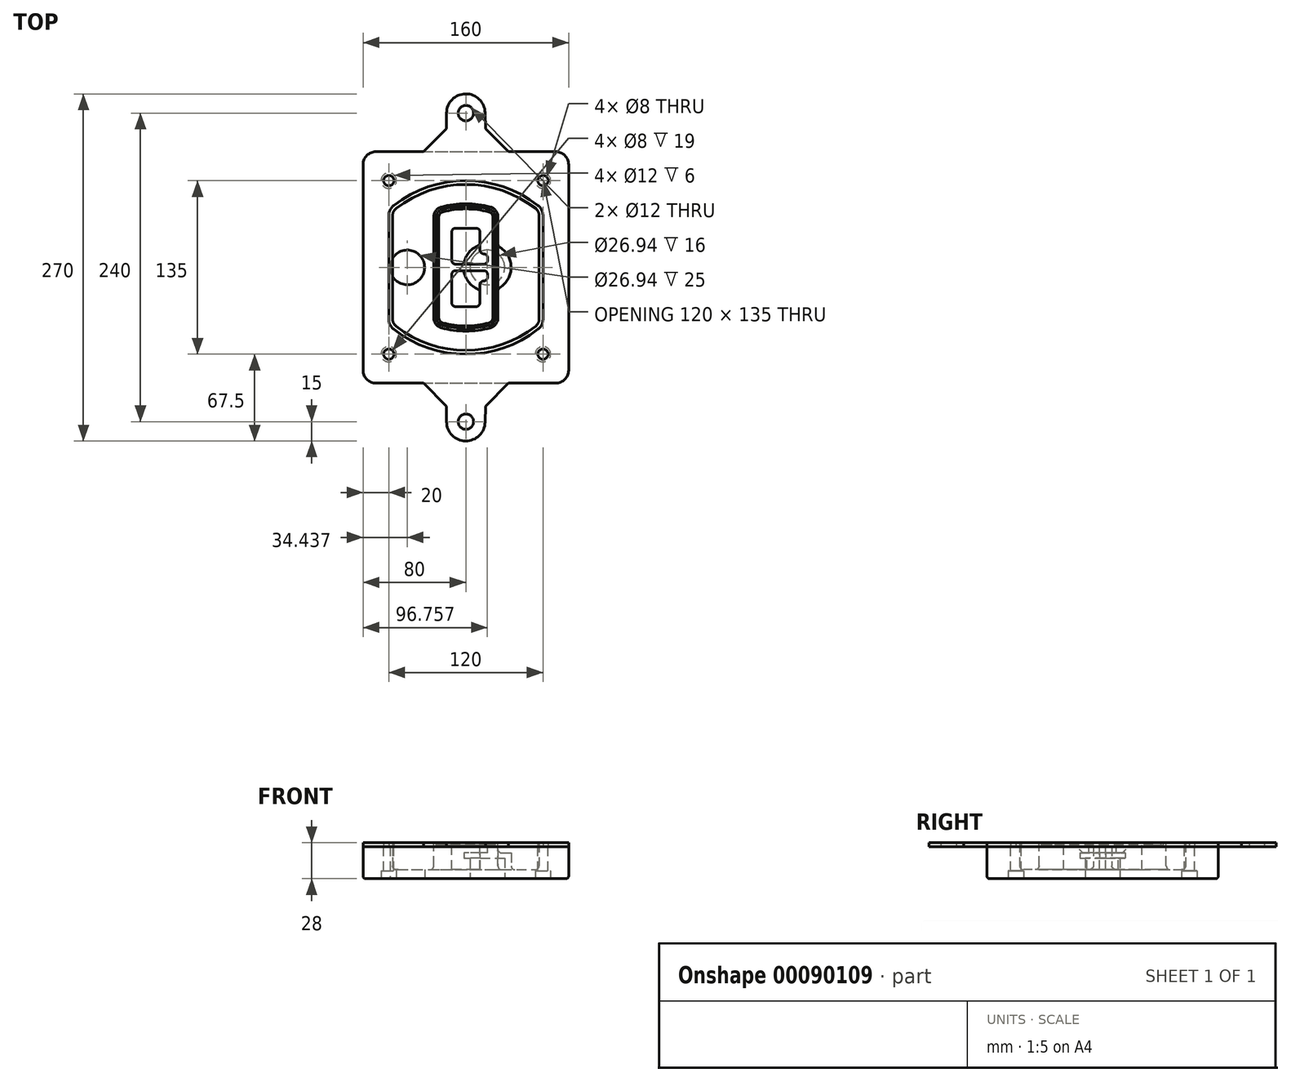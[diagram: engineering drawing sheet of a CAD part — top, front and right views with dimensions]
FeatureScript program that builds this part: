
annotation { "Feature Type Name" : "Feature", "Feature Type Description" : "" }
export const myFeature = defineFeature(function(context is Context, id is Id, definition is map)
    precondition{}
    {
        {
            var Q0;
            Q0=qCreatedBy(makeId("Top.planeOp"),FACE);
            var sketch = newSketch(context, id + "F0", { "sketchPlane" : qUnion([Q0])});
            skPoint(sketch, "E0.rect.middle", {"position": v(0, 0) * mm});
            skLineSegment(sketch, "E1.bottom", {"start": v(-70, -90) * mm, "end": v(70, -90) * mm});
            skLineSegment(sketch, "E1.top", {"start": v(-70, 90) * mm, "end": v(70, 90) * mm});
            skLineSegment(sketch, "E1.left", {"start": v(-80, -80) * mm, "end": v(-80, 80) * mm});
            skLineSegment(sketch, "E1.right", {"start": v(80, -80) * mm, "end": v(80, 80) * mm});
            skLineSegment(sketch, "E2", {"start": v(-80, 90) * mm, "end": v(80, -90) * mm, "construction": true});
            skLineSegment(sketch, "E3", {"start": v(80, 90) * mm, "end": v(-80, -90) * mm, "construction": true});
            skCircle(sketch, "E4", {"center": v(-60, 67.5) * mm, "radius": 4 * mm});
            skCircle(sketch, "E5", {"center": v(60, 67.5) * mm, "radius": 4 * mm});
            skCircle(sketch, "E6", {"center": v(60, -67.5) * mm, "radius": 4 * mm});
            skCircle(sketch, "E7", {"center": v(-60, -67.5) * mm, "radius": 4 * mm});
            skLineSegment(sketch, "E8", {"start": v(-60, 67.5) * mm, "end": v(60, 67.5) * mm, "construction": true});
            skLineSegment(sketch, "E9", {"start": v(60, 67.5) * mm, "end": v(60, -67.5) * mm, "construction": true});
            skLineSegment(sketch, "E10", {"start": v(60, -67.5) * mm, "end": v(-60, -67.5) * mm, "construction": true});
            skLineSegment(sketch, "E11", {"start": v(-60, -67.5) * mm, "end": v(-60, 67.5) * mm, "construction": true});
            skLineSegment(sketch, "E12", {"start": v(-60, 40.3) * mm, "end": v(-60, -40.3) * mm});
            skLineSegment(sketch, "E13", {"start": v(60, 40.3) * mm, "end": v(60, -40.3) * mm});
            skArc(sketch, "E14", {"start": v(56.15, 48.18) * mm, "mid": v(0, 67.5) * mm, "end": v(-56.15, 48.18) * mm});
            skArc(sketch, "E15", {"start": v(-56.15, -48.18) * mm, "mid": v(0, -67.5) * mm, "end": v(56.15, -48.18) * mm});
            skLineSegment(sketch, "E16", {"start": v(-60, 0) * mm, "end": v(60, 0) * mm, "construction": true});
            skPoint(sketch, "E17.visualSharp", {"position": v(-60, -45) * mm});
            skArc(sketch, "E17.filletArc", {"start": v(-60, -40.3) * mm, "mid": v(-58.99, -44.68) * mm, "end": v(-56.15, -48.18) * mm});
            skPoint(sketch, "E18.visualSharp", {"position": v(-60, 45) * mm});
            skArc(sketch, "E18.filletArc", {"start": v(-56.15, 48.18) * mm, "mid": v(-58.99, 44.68) * mm, "end": v(-60, 40.3) * mm});
            skPoint(sketch, "E19.visualSharp", {"position": v(60, 45) * mm});
            skArc(sketch, "E19.filletArc", {"start": v(60, 40.3) * mm, "mid": v(58.99, 44.68) * mm, "end": v(56.15, 48.18) * mm});
            skPoint(sketch, "E20.visualSharp", {"position": v(60, -45) * mm});
            skArc(sketch, "E20.filletArc", {"start": v(56.15, -48.18) * mm, "mid": v(58.99, -44.68) * mm, "end": v(60, -40.3) * mm});
            skPoint(sketch, "E21.visualSharp", {"position": v(-80, 90) * mm});
            skArc(sketch, "E21.filletArc", {"start": v(-70, 90) * mm, "mid": v(-77.07, 87.07) * mm, "end": v(-80, 80) * mm});
            skPoint(sketch, "E22.visualSharp", {"position": v(80, 90) * mm});
            skArc(sketch, "E22.filletArc", {"start": v(80, 80) * mm, "mid": v(77.07, 87.07) * mm, "end": v(70, 90) * mm});
            skPoint(sketch, "E23.visualSharp", {"position": v(80, -90) * mm});
            skArc(sketch, "E23.filletArc", {"start": v(70, -90) * mm, "mid": v(77.07, -87.07) * mm, "end": v(80, -80) * mm});
            skPoint(sketch, "E24.visualSharp", {"position": v(-80, -90) * mm});
            skArc(sketch, "E24.filletArc", {"start": v(-80, -80) * mm, "mid": v(-77.07, -87.07) * mm, "end": v(-70, -90) * mm});
            skArc(sketch, "E25.0", {"start": v(57, 40.3) * mm, "mid": v(56.3, 43.36) * mm, "end": v(54.3, 45.81) * mm});
            skLineSegment(sketch, "E25.1", {"start": v(57, 40.3) * mm, "end": v(57, -40.3) * mm});
            skArc(sketch, "E25.2", {"start": v(54.3, -45.81) * mm, "mid": v(56.3, -43.36) * mm, "end": v(57, -40.3) * mm});
            skArc(sketch, "E25.3", {"start": v(-54.3, -45.81) * mm, "mid": v(0, -64.5) * mm, "end": v(54.3, -45.81) * mm});
            skArc(sketch, "E25.4", {"start": v(-57, -40.3) * mm, "mid": v(-56.3, -43.36) * mm, "end": v(-54.3, -45.81) * mm});
            skArc(sketch, "E25.5", {"start": v(54.3, 45.81) * mm, "mid": v(0, 64.5) * mm, "end": v(-54.3, 45.81) * mm});
            skLineSegment(sketch, "E25.6", {"start": v(-57, 40.3) * mm, "end": v(-57, -40.3) * mm});
            skArc(sketch, "E25.7", {"start": v(-54.3, 45.81) * mm, "mid": v(-56.3, 43.36) * mm, "end": v(-57, 40.3) * mm});
            skArc(sketch, "E26.0", {"start": v(-58.62, 51.33) * mm, "mid": v(-62.58, 46.43) * mm, "end": v(-64, 40.3) * mm});
            skArc(sketch, "E26.1", {"start": v(58.62, 51.33) * mm, "mid": v(0, 71.5) * mm, "end": v(-58.62, 51.33) * mm});
            skArc(sketch, "E26.2", {"start": v(64, 40.3) * mm, "mid": v(62.58, 46.43) * mm, "end": v(58.62, 51.33) * mm});
            skLineSegment(sketch, "E26.3", {"start": v(64, 40.3) * mm, "end": v(64, -40.3) * mm});
            skArc(sketch, "E26.4", {"start": v(58.62, -51.33) * mm, "mid": v(62.58, -46.43) * mm, "end": v(64, -40.3) * mm});
            skLineSegment(sketch, "E26.5", {"start": v(-64, 40.3) * mm, "end": v(-64, -40.3) * mm});
            skArc(sketch, "E26.6", {"start": v(-58.62, -51.33) * mm, "mid": v(0, -71.5) * mm, "end": v(58.62, -51.33) * mm});
            skArc(sketch, "E26.7", {"start": v(-64, -40.3) * mm, "mid": v(-62.58, -46.43) * mm, "end": v(-58.62, -51.33) * mm});
            skSolve(sketch);
        }
        {
            var Q0;
            Q0=makeQuery(id+"F0.imprint","IMPRINT",FACE,{"disambiguationData":[TD([[makeQuery(id+"F0.imprint","IMPRINT",EDGE,{"derivedFrom":sQuery(id+"F0.wireOp",EDGE,"E1.bottom")}),1.0]])]});
            var Q1;
            Q1=makeQuery(id+"F0.imprint","IMPRINT",FACE,{"disambiguationData":[TD([[makeQuery(id+"F0.imprint","IMPRINT",EDGE,{"derivedFrom":sQuery(id+"F0.wireOp",EDGE,"E12")}),1.0]])]});
            var Q2;
            Q2=makeQuery(id+"F0.imprint","IMPRINT",FACE,{"disambiguationData":[TD([[makeQuery(id+"F0.imprint","IMPRINT",EDGE,{"derivedFrom":sQuery(id+"F0.wireOp",EDGE,"E25.0")}),1.0]])]});
            var Q3;
            Q3=makeQuery(id+"F0.imprint","IMPRINT",FACE,{"disambiguationData":[TD([[makeQuery(id+"F0.imprint","IMPRINT",EDGE,{"derivedFrom":sQuery(id+"F0.wireOp",EDGE,"E12")}),-1.0]])]});
            extrude(context, id + "F1", {"entities" : qUnion([Q0, Q1, Q2, Q3]), "oppositeDirection" : true, "depth" : 25 * mm});
        }
        {
            var Q0;
            Q0=makeQuery(id+"F0.imprint","IMPRINT",FACE,{"disambiguationData":[TD([[makeQuery(id+"F0.imprint","IMPRINT",EDGE,{"derivedFrom":sQuery(id+"F0.wireOp",EDGE,"E12")}),1.0]])]});
            extrude(context, id + "F2", {"entities" : qUnion([Q0]), "operationType" : NewBodyOperationType.ADD, "depth" : 3 * mm});
        }
        {
            var Q0;
            Q0=makeQuery(id+"F0.imprint","IMPRINT",FACE,{"disambiguationData":[TD([[makeQuery(id+"F0.imprint","IMPRINT",EDGE,{"derivedFrom":sQuery(id+"F0.wireOp",EDGE,"E25.0")}),1.0]])]});
            extrude(context, id + "F3", {"entities" : qUnion([Q0]), "operationType" : NewBodyOperationType.REMOVE, "oppositeDirection" : true, "depth" : 18 * mm});
        }
        {
            var Q0;
            Q0=makeQuery(id+"F2.opExtrude","CAP_FACE",FACE,{"disambiguationData":[OSD([sQuery(id+"F0.wireOp",EDGE,"E12"),sQuery(id+"F0.wireOp",EDGE,"E13"),sQuery(id+"F0.wireOp",EDGE,"E14"),sQuery(id+"F0.wireOp",EDGE,"E15"),sQuery(id+"F0.wireOp",EDGE,"E17.filletArc"),sQuery(id+"F0.wireOp",EDGE,"E18.filletArc"),sQuery(id+"F0.wireOp",EDGE,"E19.filletArc"),sQuery(id+"F0.wireOp",EDGE,"E20.filletArc"),sQuery(id+"F0.wireOp",EDGE,"E25.0"),sQuery(id+"F0.wireOp",EDGE,"E25.1"),sQuery(id+"F0.wireOp",EDGE,"E25.2"),sQuery(id+"F0.wireOp",EDGE,"E25.3"),sQuery(id+"F0.wireOp",EDGE,"E25.4"),sQuery(id+"F0.wireOp",EDGE,"E25.5"),sQuery(id+"F0.wireOp",EDGE,"E25.6"),sQuery(id+"F0.wireOp",EDGE,"E25.7")])],"isStart":false});
            var sketch = newSketch(context, id + "F4", { "sketchPlane" : qUnion([Q0])});
            skArc(sketch, "E27.0", {"start": v(-19.08, -46.97) * mm, "mid": v(0, -49.5) * mm, "end": v(19.08, -46.97) * mm});
            skArc(sketch, "E28.0", {"start": v(19.08, 46.97) * mm, "mid": v(0, 49.5) * mm, "end": v(-19.08, 46.97) * mm});
            skLineSegment(sketch, "E29", {"start": v(-25, 39.25) * mm, "end": v(-25, -39.25) * mm});
            skLineSegment(sketch, "E30", {"start": v(25, 39.25) * mm, "end": v(25, -39.25) * mm});
            skLineSegment(sketch, "E31", {"start": v(-25, 45.1) * mm, "end": v(25, 45.1) * mm, "construction": true});
            skLineSegment(sketch, "E32", {"start": v(-25, -45.1) * mm, "end": v(25, -45.1) * mm, "construction": true});
            skPoint(sketch, "E33.visualSharp", {"position": v(-25, 45.1) * mm});
            skArc(sketch, "E33.filletArc", {"start": v(-19.08, 46.97) * mm, "mid": v(-23.35, 44.11) * mm, "end": v(-25, 39.25) * mm});
            skPoint(sketch, "E34.visualSharp", {"position": v(25, 45.1) * mm});
            skArc(sketch, "E34.filletArc", {"start": v(25, 39.25) * mm, "mid": v(23.35, 44.11) * mm, "end": v(19.08, 46.97) * mm});
            skPoint(sketch, "E35.visualSharp", {"position": v(25, -45.1) * mm});
            skArc(sketch, "E35.filletArc", {"start": v(19.08, -46.97) * mm, "mid": v(23.35, -44.11) * mm, "end": v(25, -39.25) * mm});
            skPoint(sketch, "E36.visualSharp", {"position": v(-25, -45.1) * mm});
            skArc(sketch, "E36.filletArc", {"start": v(-25, -39.25) * mm, "mid": v(-23.35, -44.11) * mm, "end": v(-19.08, -46.97) * mm});
            skArc(sketch, "E37.0", {"start": v(54.3, 45.81) * mm, "mid": v(0, 64.5) * mm, "end": v(-54.3, 45.81) * mm});
            skArc(sketch, "E37.1", {"start": v(-54.3, 45.81) * mm, "mid": v(-56.3, 43.36) * mm, "end": v(-57, 40.3) * mm});
            skLineSegment(sketch, "E37.2", {"start": v(-57, 40.3) * mm, "end": v(-57, -40.3) * mm});
            skArc(sketch, "E37.3", {"start": v(-57, -40.3) * mm, "mid": v(-56.3, -43.36) * mm, "end": v(-54.3, -45.81) * mm});
            skArc(sketch, "E37.4", {"start": v(-54.3, -45.81) * mm, "mid": v(0, -64.5) * mm, "end": v(54.3, -45.81) * mm});
            skArc(sketch, "E37.5", {"start": v(54.3, -45.81) * mm, "mid": v(56.3, -43.36) * mm, "end": v(57, -40.3) * mm});
            skLineSegment(sketch, "E37.6", {"start": v(57, 40.3) * mm, "end": v(57, -40.3) * mm});
            skArc(sketch, "E37.7", {"start": v(57, 40.3) * mm, "mid": v(56.3, 43.36) * mm, "end": v(54.3, 45.81) * mm});
            skLineSegment(sketch, "E38.0", {"start": v(23, 39.25) * mm, "end": v(23, -39.25) * mm});
            skArc(sketch, "E38.1", {"start": v(18.56, -45.04) * mm, "mid": v(21.76, -42.9) * mm, "end": v(23, -39.25) * mm});
            skArc(sketch, "E38.2", {"start": v(-18.56, -45.04) * mm, "mid": v(0, -47.5) * mm, "end": v(18.56, -45.04) * mm});
            skArc(sketch, "E38.3", {"start": v(-23, -39.25) * mm, "mid": v(-21.76, -42.9) * mm, "end": v(-18.56, -45.04) * mm});
            skLineSegment(sketch, "E38.4", {"start": v(-23, 39.25) * mm, "end": v(-23, -39.25) * mm});
            skArc(sketch, "E38.5", {"start": v(23, 39.25) * mm, "mid": v(21.76, 42.9) * mm, "end": v(18.56, 45.04) * mm});
            skArc(sketch, "E38.6", {"start": v(-18.56, 45.04) * mm, "mid": v(-21.76, 42.9) * mm, "end": v(-23, 39.25) * mm});
            skArc(sketch, "E38.7", {"start": v(18.56, 45.04) * mm, "mid": v(0, 47.5) * mm, "end": v(-18.56, 45.04) * mm});
            skArc(sketch, "E39.0", {"start": v(21, 39.25) * mm, "mid": v(20.18, 41.68) * mm, "end": v(18.04, 43.1) * mm});
            skLineSegment(sketch, "E39.1", {"start": v(21, 39.25) * mm, "end": v(21, -39.25) * mm});
            skArc(sketch, "E39.2", {"start": v(18.04, -43.1) * mm, "mid": v(20.18, -41.68) * mm, "end": v(21, -39.25) * mm});
            skArc(sketch, "E39.3", {"start": v(-18.04, -43.1) * mm, "mid": v(0, -45.5) * mm, "end": v(18.04, -43.1) * mm});
            skArc(sketch, "E39.4", {"start": v(-21, -39.25) * mm, "mid": v(-20.18, -41.68) * mm, "end": v(-18.04, -43.1) * mm});
            skArc(sketch, "E39.5", {"start": v(18.04, 43.1) * mm, "mid": v(0, 45.5) * mm, "end": v(-18.04, 43.1) * mm});
            skLineSegment(sketch, "E39.6", {"start": v(-21, 39.25) * mm, "end": v(-21, -39.25) * mm});
            skArc(sketch, "E39.7", {"start": v(-18.04, 43.1) * mm, "mid": v(-20.18, 41.68) * mm, "end": v(-21, 39.25) * mm});
            skLineSegment(sketch, "E40", {"start": v(-25, 0) * mm, "end": v(25, 0) * mm, "construction": true});
            skLineSegment(sketch, "E41", {"start": v(-11, 5.5) * mm, "end": v(-11, 27.5) * mm});
            skLineSegment(sketch, "E42", {"start": v(-8, 30.5) * mm, "end": v(8, 30.5) * mm});
            skLineSegment(sketch, "E43", {"start": v(11, 27.5) * mm, "end": v(11, 13.5) * mm});
            skLineSegment(sketch, "E44", {"start": v(14, 10.5) * mm, "end": v(14, 10.5) * mm});
            skLineSegment(sketch, "E45", {"start": v(17, 7.5) * mm, "end": v(17, 5.5) * mm});
            skLineSegment(sketch, "E46", {"start": v(14, 2.5) * mm, "end": v(-8, 2.5) * mm});
            skPoint(sketch, "E47.visualSharp", {"position": v(-11, 30.5) * mm});
            skArc(sketch, "E47.filletArc", {"start": v(-8, 30.5) * mm, "mid": v(-10.12, 29.62) * mm, "end": v(-11, 27.5) * mm});
            skPoint(sketch, "E48.visualSharp", {"position": v(11, 30.5) * mm});
            skArc(sketch, "E48.filletArc", {"start": v(11, 27.5) * mm, "mid": v(10.12, 29.62) * mm, "end": v(8, 30.5) * mm});
            skPoint(sketch, "E49.visualSharp", {"position": v(11, 10.5) * mm});
            skArc(sketch, "E49.filletArc", {"start": v(11, 13.5) * mm, "mid": v(11.88, 11.38) * mm, "end": v(14, 10.5) * mm});
            skPoint(sketch, "E50.visualSharp", {"position": v(17, 10.5) * mm});
            skArc(sketch, "E50.filletArc", {"start": v(17, 7.5) * mm, "mid": v(16.12, 9.62) * mm, "end": v(14, 10.5) * mm});
            skPoint(sketch, "E51.visualSharp", {"position": v(17, 2.5) * mm});
            skArc(sketch, "E51.filletArc", {"start": v(14, 2.5) * mm, "mid": v(16.12, 3.38) * mm, "end": v(17, 5.5) * mm});
            skPoint(sketch, "E52.visualSharp", {"position": v(-11, 2.5) * mm});
            skArc(sketch, "E52.filletArc", {"start": v(-11, 5.5) * mm, "mid": v(-10.12, 3.38) * mm, "end": v(-8, 2.5) * mm});
            skLineSegment(sketch, "E53.0.MirrorCS", {"start": v(14, -2.5) * mm, "end": v(-8, -2.5) * mm});
            skArc(sketch, "E54.0.MirrorCS", {"start": v(-11, -5.5) * mm, "mid": v(-10.12, -3.38) * mm, "end": v(-8, -2.5) * mm});
            skLineSegment(sketch, "E55.0.MirrorCS", {"start": v(-11, -5.5) * mm, "end": v(-11, -27.5) * mm});
            skArc(sketch, "E56.0.MirrorCS", {"start": v(-8, -30.5) * mm, "mid": v(-10.12, -29.62) * mm, "end": v(-11, -27.5) * mm});
            skLineSegment(sketch, "E57.0.MirrorCS", {"start": v(-8, -30.5) * mm, "end": v(8, -30.5) * mm});
            skArc(sketch, "E58.0.MirrorCS", {"start": v(11, -27.5) * mm, "mid": v(10.12, -29.62) * mm, "end": v(8, -30.5) * mm});
            skLineSegment(sketch, "E59.0.MirrorCS", {"start": v(11, -27.5) * mm, "end": v(11, -13.5) * mm});
            skArc(sketch, "E60.0.MirrorCS", {"start": v(11, -13.5) * mm, "mid": v(11.88, -11.38) * mm, "end": v(14, -10.5) * mm});
            skArc(sketch, "E61.0.MirrorCS", {"start": v(17, -7.5) * mm, "mid": v(16.12, -9.62) * mm, "end": v(14, -10.5) * mm});
            skLineSegment(sketch, "E62.0.MirrorCS", {"start": v(17, -7.5) * mm, "end": v(17, -5.5) * mm});
            skArc(sketch, "E63.0.MirrorCS", {"start": v(14, -2.5) * mm, "mid": v(16.12, -3.38) * mm, "end": v(17, -5.5) * mm});
            skSolve(sketch);
        }
        {
            var Q0;
            Q0=makeQuery(id+"F4.imprint","IMPRINT",FACE,{"disambiguationData":[TD([[makeQuery(id+"F4.imprint","IMPRINT",EDGE,{"derivedFrom":sQuery(id+"F4.wireOp",EDGE,"E27.0")}),1.0]])]});
            var Q1;
            Q1=makeQuery(id+"F4.imprint","IMPRINT",FACE,{"disambiguationData":[TD([[makeQuery(id+"F4.imprint","IMPRINT",EDGE,{"derivedFrom":sQuery(id+"F4.wireOp",EDGE,"E38.0")}),-1.0]])]});
            var Q2;
            Q2=makeQuery(id+"F4.imprint","IMPRINT",FACE,{"disambiguationData":[TD([[makeQuery(id+"F4.imprint","IMPRINT",EDGE,{"derivedFrom":sQuery(id+"F4.wireOp",EDGE,"E39.0")}),1.0]])]});
            extrude(context, id + "F5", {"entities" : qUnion([Q0, Q1, Q2]), "operationType" : NewBodyOperationType.ADD, "endBound" : BoundingType.UP_TO_NEXT, "oppositeDirection" : true, "depth" : 25 * mm});
        }
        {
            var Q0;
            Q0=makeQuery(id+"F4.imprint","IMPRINT",FACE,{"disambiguationData":[TD([[makeQuery(id+"F4.imprint","IMPRINT",EDGE,{"derivedFrom":sQuery(id+"F4.wireOp",EDGE,"E38.0")}),-1.0]])]});
            extrude(context, id + "F6", {"entities" : qUnion([Q0]), "operationType" : NewBodyOperationType.REMOVE, "oppositeDirection" : true, "depth" : 2 * mm});
        }
        {
            var Q0;
            Q0=makeQuery(id+"F1.opExtrude","CAP_FACE",FACE,{"disambiguationData":[OSD([sQuery(id+"F0.wireOp",EDGE,"E1.bottom"),sQuery(id+"F0.wireOp",EDGE,"E1.top"),sQuery(id+"F0.wireOp",EDGE,"E1.left"),sQuery(id+"F0.wireOp",EDGE,"E1.right"),sQuery(id+"F0.wireOp",EDGE,"E4"),sQuery(id+"F0.wireOp",EDGE,"E5"),sQuery(id+"F0.wireOp",EDGE,"E6"),sQuery(id+"F0.wireOp",EDGE,"E7"),sQuery(id+"F0.wireOp",EDGE,"E21.filletArc"),sQuery(id+"F0.wireOp",EDGE,"E22.filletArc"),sQuery(id+"F0.wireOp",EDGE,"E23.filletArc"),sQuery(id+"F0.wireOp",EDGE,"E24.filletArc")])],"isStart":false});
            var sketch = newSketch(context, id + "F7", { "sketchPlane" : qUnion([Q0])});
            skCircle(sketch, "E64", {"center": v(16.76, 0) * mm, "radius": 13.47 * mm});
            skCircle(sketch, "E65", {"center": v(-45.56, 0) * mm, "radius": 13.47 * mm});
            skLineSegment(sketch, "E66", {"start": v(80, 0) * mm, "end": v(-80, 0) * mm});
            skCircle(sketch, "E67", {"center": v(16.76, 0) * mm, "radius": 18.47 * mm});
            skCircle(sketch, "E68", {"center": v(60, -67.5) * mm, "radius": 6 * mm});
            skCircle(sketch, "E69", {"center": v(-60, -67.5) * mm, "radius": 6 * mm});
            skCircle(sketch, "E70", {"center": v(-60, 67.5) * mm, "radius": 6 * mm});
            skCircle(sketch, "E71", {"center": v(60, 67.5) * mm, "radius": 6 * mm});
            skSolve(sketch);
        }
        {
            var Q0;
            {var subQ1=sQuery(id+"F7.wireOp",EDGE,"E66");var subQ4=sQuery(id+"F7.wireOp",EDGE,"E64");var subQ6=makeQuery(id+"F7.imprint","INTERSECT",VERTEX,{"disambiguationData":[OD(0.0)],"derivedFrom":[subQ4,subQ1]});Q0=makeQuery(id+"F7.imprint","IMPRINT",FACE,{"disambiguationData":[TD([[makeQuery(id+"F7.imprint","IMPRINT",EDGE,{"disambiguationData":[TD([[subQ6,-1.0]])],"derivedFrom":subQ4}),-1.0]])]});}
            var Q1;
            {var subQ0=sQuery(id+"F7.wireOp",EDGE,"E66");var subQ1=sQuery(id+"F7.wireOp",EDGE,"E64");var subQ3=makeQuery(id+"F7.imprint","INTERSECT",VERTEX,{"disambiguationData":[OD(0.0)],"derivedFrom":[subQ1,subQ0]});Q1=makeQuery(id+"F7.imprint","IMPRINT",FACE,{"disambiguationData":[TD([[makeQuery(id+"F7.imprint","IMPRINT",EDGE,{"disambiguationData":[TD([[subQ3,-1.0]])],"derivedFrom":subQ1}),1.0]])]});}
            var Q2;
            {var subQ0=sQuery(id+"F7.wireOp",EDGE,"E66");var subQ1=sQuery(id+"F7.wireOp",EDGE,"E64");var subQ3=makeQuery(id+"F7.imprint","INTERSECT",VERTEX,{"disambiguationData":[OD(0.0)],"derivedFrom":[subQ1,subQ0]});Q2=makeQuery(id+"F7.imprint","IMPRINT",FACE,{"disambiguationData":[TD([[makeQuery(id+"F7.imprint","IMPRINT",EDGE,{"disambiguationData":[TD([[subQ3,1.0]])],"derivedFrom":subQ1}),1.0]])]});}
            var Q3;
            {var subQ1=sQuery(id+"F7.wireOp",EDGE,"E66");var subQ4=sQuery(id+"F7.wireOp",EDGE,"E64");var subQ6=makeQuery(id+"F7.imprint","INTERSECT",VERTEX,{"disambiguationData":[OD(0.0)],"derivedFrom":[subQ4,subQ1]});Q3=makeQuery(id+"F7.imprint","IMPRINT",FACE,{"disambiguationData":[TD([[makeQuery(id+"F7.imprint","IMPRINT",EDGE,{"disambiguationData":[TD([[subQ6,1.0]])],"derivedFrom":subQ4}),-1.0]])]});}
            extrude(context, id + "F8", {"entities" : qUnion([Q0, Q1, Q2, Q3]), "operationType" : NewBodyOperationType.ADD, "oppositeDirection" : true, "depth" : 20 * mm});
        }
        {
            var Q0;
            {var subQ0=sQuery(id+"F7.wireOp",EDGE,"E66");var subQ1=sQuery(id+"F7.wireOp",EDGE,"E64");var subQ3=makeQuery(id+"F7.imprint","INTERSECT",VERTEX,{"disambiguationData":[OD(0.0)],"derivedFrom":[subQ1,subQ0]});Q0=makeQuery(id+"F7.imprint","IMPRINT",FACE,{"disambiguationData":[TD([[makeQuery(id+"F7.imprint","IMPRINT",EDGE,{"disambiguationData":[TD([[subQ3,-1.0]])],"derivedFrom":subQ1}),1.0]])]});}
            var Q1;
            {var subQ0=sQuery(id+"F7.wireOp",EDGE,"E66");var subQ1=sQuery(id+"F7.wireOp",EDGE,"E64");var subQ3=makeQuery(id+"F7.imprint","INTERSECT",VERTEX,{"disambiguationData":[OD(0.0)],"derivedFrom":[subQ1,subQ0]});Q1=makeQuery(id+"F7.imprint","IMPRINT",FACE,{"disambiguationData":[TD([[makeQuery(id+"F7.imprint","IMPRINT",EDGE,{"disambiguationData":[TD([[subQ3,1.0]])],"derivedFrom":subQ1}),1.0]])]});}
            extrude(context, id + "F9", {"entities" : qUnion([Q0, Q1]), "operationType" : NewBodyOperationType.REMOVE, "oppositeDirection" : true, "depth" : 16 * mm});
        }
        {
            var Q0;
            {var subQ0=sQuery(id+"F7.wireOp",EDGE,"E66");var subQ1=sQuery(id+"F7.wireOp",EDGE,"E65");var subQ3=makeQuery(id+"F7.imprint","INTERSECT",VERTEX,{"disambiguationData":[OD(0.0)],"derivedFrom":[subQ1,subQ0]});Q0=makeQuery(id+"F7.imprint","IMPRINT",FACE,{"disambiguationData":[TD([[makeQuery(id+"F7.imprint","IMPRINT",EDGE,{"disambiguationData":[TD([[subQ3,-1.0]])],"derivedFrom":subQ1}),1.0]])]});}
            var Q1;
            {var subQ0=sQuery(id+"F7.wireOp",EDGE,"E66");var subQ1=sQuery(id+"F7.wireOp",EDGE,"E65");var subQ3=makeQuery(id+"F7.imprint","INTERSECT",VERTEX,{"disambiguationData":[OD(0.0)],"derivedFrom":[subQ1,subQ0]});Q1=makeQuery(id+"F7.imprint","IMPRINT",FACE,{"disambiguationData":[TD([[makeQuery(id+"F7.imprint","IMPRINT",EDGE,{"disambiguationData":[TD([[subQ3,1.0]])],"derivedFrom":subQ1}),1.0]])]});}
            extrude(context, id + "F10", {"entities" : qUnion([Q0, Q1]), "operationType" : NewBodyOperationType.REMOVE, "oppositeDirection" : true, "depth" : 25 * mm});
        }
        {
            var Q0;
            Q0=makeQuery(id+"F7.imprint","IMPRINT",FACE,{"disambiguationData":[TD([[makeQuery(id+"F7.imprint","IMPRINT",EDGE,{"derivedFrom":sQuery(id+"F7.wireOp",EDGE,"E68")}),1.0]])]});
            var Q1;
            Q1=makeQuery(id+"F7.imprint","IMPRINT",FACE,{"disambiguationData":[TD([[makeQuery(id+"F7.imprint","IMPRINT",EDGE,{"derivedFrom":makeQuery(id+"F1.opExtrude","CAP_EDGE",EDGE,{"disambiguationData":[OSD([sQuery(id+"F0.wireOp",EDGE,"E5")])],"isStart":false})}),-1.0]])]});
            var Q2;
            Q2=makeQuery(id+"F7.imprint","IMPRINT",FACE,{"disambiguationData":[TD([[makeQuery(id+"F7.imprint","IMPRINT",EDGE,{"derivedFrom":sQuery(id+"F7.wireOp",EDGE,"E69")}),1.0]])]});
            var Q3;
            Q3=makeQuery(id+"F7.imprint","IMPRINT",FACE,{"disambiguationData":[TD([[makeQuery(id+"F7.imprint","IMPRINT",EDGE,{"derivedFrom":makeQuery(id+"F1.opExtrude","CAP_EDGE",EDGE,{"disambiguationData":[OSD([sQuery(id+"F0.wireOp",EDGE,"E4")])],"isStart":false})}),-1.0]])]});
            var Q4;
            Q4=makeQuery(id+"F7.imprint","IMPRINT",FACE,{"disambiguationData":[TD([[makeQuery(id+"F7.imprint","IMPRINT",EDGE,{"derivedFrom":sQuery(id+"F7.wireOp",EDGE,"E70")}),1.0]])]});
            var Q5;
            Q5=makeQuery(id+"F7.imprint","IMPRINT",FACE,{"disambiguationData":[TD([[makeQuery(id+"F7.imprint","IMPRINT",EDGE,{"derivedFrom":makeQuery(id+"F1.opExtrude","CAP_EDGE",EDGE,{"disambiguationData":[OSD([sQuery(id+"F0.wireOp",EDGE,"E7")])],"isStart":false})}),-1.0]])]});
            var Q6;
            Q6=makeQuery(id+"F7.imprint","IMPRINT",FACE,{"disambiguationData":[TD([[makeQuery(id+"F7.imprint","IMPRINT",EDGE,{"derivedFrom":sQuery(id+"F7.wireOp",EDGE,"E71")}),1.0]])]});
            var Q7;
            Q7=makeQuery(id+"F7.imprint","IMPRINT",FACE,{"disambiguationData":[TD([[makeQuery(id+"F7.imprint","IMPRINT",EDGE,{"derivedFrom":makeQuery(id+"F1.opExtrude","CAP_EDGE",EDGE,{"disambiguationData":[OSD([sQuery(id+"F0.wireOp",EDGE,"E6")])],"isStart":false})}),-1.0]])]});
            extrude(context, id + "F11", {"entities" : qUnion([Q0, Q1, Q2, Q3, Q4, Q5, Q6, Q7]), "operationType" : NewBodyOperationType.REMOVE, "oppositeDirection" : true, "depth" : 6 * mm});
        }
        {
            var Q0;
            Q0=makeQuery(id+"F9.boolean.opBoolean","COPY",FACE,{"derivedFrom":makeQuery(id+"F9.opExtrude","CAP_FACE",FACE,{"disambiguationData":[OSD([sQuery(id+"F7.wireOp",EDGE,"E64")])],"isStart":false})});
            var sketch = newSketch(context, id + "F12", { "sketchPlane" : qUnion([Q0])});
            skArc(sketch, "E72.0", {"start": v(11, 17.55) * mm, "mid": v(2.57, 11.82) * mm, "end": v(-1.54, 2.5) * mm});
            skArc(sketch, "E72.1", {"start": v(-1.54, -2.5) * mm, "mid": v(2.57, -11.82) * mm, "end": v(11, -17.55) * mm});
            skLineSegment(sketch, "E73", {"start": v(-1.54, -2.5) * mm, "end": v(14, -2.5) * mm});
            skLineSegment(sketch, "E74.0", {"start": v(14, 2.5) * mm, "end": v(-1.54, 2.5) * mm});
            skArc(sketch, "E74.1", {"start": v(14, 2.5) * mm, "mid": v(16.12, 3.38) * mm, "end": v(17, 5.5) * mm});
            skLineSegment(sketch, "E74.2", {"start": v(17, 7.5) * mm, "end": v(17, 5.5) * mm});
            skArc(sketch, "E74.3", {"start": v(17, 7.5) * mm, "mid": v(16.12, 9.62) * mm, "end": v(14, 10.5) * mm});
            skArc(sketch, "E74.4", {"start": v(11, 13.5) * mm, "mid": v(11.88, 11.38) * mm, "end": v(14, 10.5) * mm});
            skLineSegment(sketch, "E74.5", {"start": v(11, 17.55) * mm, "end": v(11, 13.5) * mm});
            skLineSegment(sketch, "E74.7", {"start": v(14, -2.5) * mm, "end": v(-1.54, -2.5) * mm});
            skArc(sketch, "E74.8", {"start": v(14, -2.5) * mm, "mid": v(16.12, -3.38) * mm, "end": v(17, -5.5) * mm});
            skLineSegment(sketch, "E74.9", {"start": v(17, -7.5) * mm, "end": v(17, -5.5) * mm});
            skArc(sketch, "E74.10", {"start": v(17, -7.5) * mm, "mid": v(16.12, -9.62) * mm, "end": v(14, -10.5) * mm});
            skArc(sketch, "E74.11", {"start": v(11, -13.5) * mm, "mid": v(11.88, -11.38) * mm, "end": v(14, -10.5) * mm});
            skLineSegment(sketch, "E74.12", {"start": v(11, -17.55) * mm, "end": v(11, -13.5) * mm});
            skPoint(sketch, "E75.orphan", {"position": v(11, -27.5) * mm});
            skPoint(sketch, "E76.orphan", {"position": v(-8, -2.5) * mm});
            skPoint(sketch, "E77.orphan", {"position": v(-8, 2.5) * mm});
            skPoint(sketch, "E78.orphan", {"position": v(11, 27.5) * mm});
            skSolve(sketch);
        }
        {
            var Q0;
            {var subQ7=sQuery(id+"F12.wireOp",EDGE,"E72.0");var subQ14=sQuery(id+"F12.wireOp",EDGE,"E72.1");var subQ16=sQuery(id+"F12.wireOp",EDGE,"E74.1");var subQ18=sQuery(id+"F12.wireOp",EDGE,"E74.8");Q0=qUnion([makeQuery(id+"F12.imprint","IMPRINT",FACE,{"disambiguationData":[TD([[makeQuery(id+"F12.imprint","IMPRINT",EDGE,{"derivedFrom":subQ7}),1.0]])]}),makeQuery(id+"F12.imprint","IMPRINT",FACE,{"disambiguationData":[TD([[makeQuery(id+"F12.imprint","IMPRINT",EDGE,{"derivedFrom":subQ14}),1.0]])]}),makeQuery(id+"F12.imprint","IMPRINT",FACE,{"disambiguationData":[TD([[makeQuery(id+"F12.imprint","IMPRINT",EDGE,{"derivedFrom":subQ16}),1.0]])]}),makeQuery(id+"F12.imprint","IMPRINT",FACE,{"disambiguationData":[TD([[makeQuery(id+"F12.imprint","IMPRINT",EDGE,{"derivedFrom":subQ18}),-1.0]])]})]);}
            var Q1;
            Q1=makeQuery(id+"F5.boolean.opBoolean","SPLIT",FACE,{"disambiguationData":[TD([makeQuery(id+"F5.opExtrude","SWEPT_FACE",FACE,{"disambiguationData":[OSD([sQuery(id+"F4.wireOp",EDGE,"E41")])]})])],"derivedFrom":makeQuery(id+"F3.boolean.opBoolean","COPY",FACE,{"derivedFrom":makeQuery(id+"F3.opExtrude","CAP_FACE",FACE,{"disambiguationData":[OSD([sQuery(id+"F0.wireOp",EDGE,"E25.0"),sQuery(id+"F0.wireOp",EDGE,"E25.1"),sQuery(id+"F0.wireOp",EDGE,"E25.2"),sQuery(id+"F0.wireOp",EDGE,"E25.3"),sQuery(id+"F0.wireOp",EDGE,"E25.4"),sQuery(id+"F0.wireOp",EDGE,"E25.5"),sQuery(id+"F0.wireOp",EDGE,"E25.6"),sQuery(id+"F0.wireOp",EDGE,"E25.7")])],"isStart":false})})});
            extrude(context, id + "F13", {"entities" : qUnion([Q0]), "operationType" : NewBodyOperationType.REMOVE, "endBound" : BoundingType.UP_TO_SURFACE, "endBoundEntityFace" : qUnion([Q1]), "depth" : 25 * mm});
        }
        {
            var Q0;
            Q0=makeQuery(id+"F3.boolean.opBoolean","COPY",EDGE,{"derivedFrom":makeQuery(id+"F3.opExtrude","CAP_EDGE",EDGE,{"disambiguationData":[OSD([sQuery(id+"F0.wireOp",EDGE,"E25.6")])],"isStart":false})});
            var Q1;
            Q1=makeQuery(id+"F8.boolean.opBoolean","INTERSECT",EDGE,{"derivedFrom":[makeQuery(id+"F5.opExtrude","SWEPT_FACE",FACE,{"disambiguationData":[OSD([sQuery(id+"F4.wireOp",EDGE,"E30")])]}),makeQuery(id+"F8.opExtrude","CAP_FACE",FACE,{"disambiguationData":[OSD([sQuery(id+"F7.wireOp",EDGE,"E67")])],"isStart":false})]});
            var Q2;
            Q2=makeQuery(id+"F8.boolean.opBoolean","INTERSECT",EDGE,{"disambiguationData":[OD(1.0)],"derivedFrom":[makeQuery(id+"F5.opExtrude","SWEPT_FACE",FACE,{"disambiguationData":[OSD([sQuery(id+"F4.wireOp",EDGE,"E30")])]}),makeQuery(id+"F8.opExtrude","SWEPT_FACE",FACE,{"disambiguationData":[OSD([sQuery(id+"F7.wireOp",EDGE,"E67")])]})]});
            var Q3;
            {var subQ0=sQuery(id+"F4.wireOp",EDGE,"E30");Q3=makeQuery(id+"F8.boolean.opBoolean","SPLIT",EDGE,{"disambiguationData":[TD([makeQuery(id+"F5.opExtrude","SWEPT_FACE",FACE,{"disambiguationData":[OSD([sQuery(id+"F4.wireOp",EDGE,"E35.filletArc")])]})])],"derivedFrom":makeQuery(id+"F5.opExtrude","CAP_EDGE",EDGE,{"disambiguationData":[OSD([subQ0])],"isStart":false})});}
            var Q4;
            {var subQ0=sQuery(id+"F0.wireOp",EDGE,"E25.7");var subQ1=sQuery(id+"F0.wireOp",EDGE,"E25.1");var subQ2=sQuery(id+"F0.wireOp",EDGE,"E25.6");var subQ3=sQuery(id+"F0.wireOp",EDGE,"E25.5");var subQ4=sQuery(id+"F0.wireOp",EDGE,"E25.4");var subQ5=sQuery(id+"F0.wireOp",EDGE,"E25.0");var subQ6=sQuery(id+"F0.wireOp",EDGE,"E25.2");var subQ7=sQuery(id+"F0.wireOp",EDGE,"E25.3");Q4=makeQuery(id+"F8.boolean.opBoolean","INTERSECT",EDGE,{"derivedFrom":[makeQuery(id+"F5.boolean.opBoolean","SPLIT",FACE,{"disambiguationData":[TD([makeQuery(id+"F2.opExtrude","SWEPT_FACE",FACE,{"disambiguationData":[OSD([subQ5])]})])],"derivedFrom":makeQuery(id+"F3.boolean.opBoolean","COPY",FACE,{"derivedFrom":makeQuery(id+"F3.opExtrude","CAP_FACE",FACE,{"disambiguationData":[OSD([subQ5,subQ1,subQ6,subQ7,subQ4,subQ3,subQ2,subQ0])],"isStart":false})})}),makeQuery(id+"F8.opExtrude","SWEPT_FACE",FACE,{"disambiguationData":[OSD([sQuery(id+"F7.wireOp",EDGE,"E67")])]})]});}
            var Q5;
            Q5=makeQuery(id+"F8.boolean.opBoolean","INTERSECT",EDGE,{"disambiguationData":[OD(0.0)],"derivedFrom":[makeQuery(id+"F5.opExtrude","SWEPT_FACE",FACE,{"disambiguationData":[OSD([sQuery(id+"F4.wireOp",EDGE,"E30")])]}),makeQuery(id+"F8.opExtrude","SWEPT_FACE",FACE,{"disambiguationData":[OSD([sQuery(id+"F7.wireOp",EDGE,"E67")])]})]});
            fillet(context, id + "F14", {"entities" : qUnion([Q0, Q1, Q2, Q3, Q4, Q5]), "radius" : 3 * mm, "tangentPropagation" : true, "allowEdgeOverflow" : false});
        }
        {
            var Q0;
            Q0=makeQuery(id+"F1.opExtrude","CAP_EDGE",EDGE,{"disambiguationData":[OSD([sQuery(id+"F0.wireOp",EDGE,"E1.bottom")])],"isStart":false});
            fillet(context, id + "F15", {"entities" : qUnion([Q0]), "radius" : 2 * mm, "tangentPropagation" : true, "allowEdgeOverflow" : false});
        }
        {
            var Q0;
            {var subQ0=sQuery(id+"F0.wireOp",EDGE,"E22.filletArc");var subQ1=sQuery(id+"F0.wireOp",EDGE,"E7");var subQ2=sQuery(id+"F0.wireOp",EDGE,"E6");var subQ3=sQuery(id+"F0.wireOp",EDGE,"E5");var subQ4=sQuery(id+"F0.wireOp",EDGE,"E4");var subQ5=sQuery(id+"F0.wireOp",EDGE,"E1.bottom");var subQ6=sQuery(id+"F0.wireOp",EDGE,"E21.filletArc");var subQ7=sQuery(id+"F0.wireOp",EDGE,"E1.top");var subQ8=sQuery(id+"F0.wireOp",EDGE,"E1.left");var subQ9=sQuery(id+"F0.wireOp",EDGE,"E1.right");var subQ10=sQuery(id+"F0.wireOp",EDGE,"E23.filletArc");var subQ11=sQuery(id+"F0.wireOp",EDGE,"E24.filletArc");Q0=makeQuery(id+"F2.boolean.opBoolean","SPLIT",FACE,{"disambiguationData":[TD([makeQuery(id+"F1.opExtrude","SWEPT_FACE",FACE,{"disambiguationData":[OSD([subQ5])]})])],"derivedFrom":makeQuery(id+"F1.opExtrude","CAP_FACE",FACE,{"disambiguationData":[OSD([subQ5,subQ7,subQ8,subQ9,subQ4,subQ3,subQ2,subQ1,subQ6,subQ0,subQ10,subQ11])],"isStart":true})});}
            var sketch = newSketch(context, id + "F16", { "sketchPlane" : qUnion([Q0])});
            skLineSegment(sketch, "E79", {"start": v(0, 90) * mm, "end": v(0, 120) * mm, "construction": true});
            skCircle(sketch, "E80", {"center": v(0, 120) * mm, "radius": 6 * mm});
            skArc(sketch, "E81", {"start": v(15, 120.32) * mm, "mid": v(-0.16, 135) * mm, "end": v(-15, 120) * mm});
            skLineSegment(sketch, "E82", {"start": v(-15, 120) * mm, "end": v(-15, 108) * mm});
            skLineSegment(sketch, "E83", {"start": v(15, 120.32) * mm, "end": v(15.26, 108) * mm});
            skLineSegment(sketch, "E84", {"start": v(-15, 108) * mm, "end": v(-33, 90) * mm});
            skLineSegment(sketch, "E85", {"start": v(15.26, 108) * mm, "end": v(33.26, 90) * mm});
            skLineSegment(sketch, "E86", {"start": v(-80, 0) * mm, "end": v(80, 0) * mm, "construction": true});
            skLineSegment(sketch, "E87.MirrorCS", {"start": v(-15, -108) * mm, "end": v(-33, -90) * mm});
            skLineSegment(sketch, "E88.MirrorCS", {"start": v(-15, -120) * mm, "end": v(-15, -108) * mm});
            skArc(sketch, "E89.MirrorCS", {"start": v(15, -120.32) * mm, "mid": v(-0.16, -135) * mm, "end": v(-15, -120) * mm});
            skLineSegment(sketch, "E90.MirrorCS", {"start": v(15, -120.32) * mm, "end": v(15.26, -108) * mm});
            skLineSegment(sketch, "E91.MirrorCS", {"start": v(15.26, -108) * mm, "end": v(33.26, -90) * mm});
            skLineSegment(sketch, "E92.MirrorCS", {"start": v(0, -90) * mm, "end": v(0, -120) * mm, "construction": true});
            skCircle(sketch, "E93.MirrorC", {"center": v(0, -120) * mm, "radius": 6 * mm});
            skSolve(sketch);
        }
        {
            var Q0;
            Q0=makeQuery(id+"F16.imprint","IMPRINT",FACE,{"disambiguationData":[TD([[makeQuery(id+"F16.imprint","IMPRINT",EDGE,{"derivedFrom":sQuery(id+"F16.wireOp",EDGE,"E80")}),-1.0]])]});
            var Q1;
            Q1=makeQuery(id+"F16.imprint","IMPRINT",FACE,{"disambiguationData":[TD([[makeQuery(id+"F16.imprint","IMPRINT",EDGE,{"derivedFrom":makeQuery(id+"F1.opExtrude","CAP_EDGE",EDGE,{"disambiguationData":[OSD([sQuery(id+"F0.wireOp",EDGE,"E1.left")])],"isStart":true})}),-1.0]])]});
            var Q2;
            {var subQ0=sQuery(id+"F16.wireOp",EDGE,"E87.MirrorCS");Q2=makeQuery(id+"F16.imprint","IMPRINT",FACE,{"disambiguationData":[TD([[makeQuery(id+"F16.imprint","IMPRINT",EDGE,{"derivedFrom":subQ0}),-1.0]])]});}
            var Q3;
            Q3=makeQuery(id+"F2.opExtrude","CAP_FACE",FACE,{"disambiguationData":[OSD([sQuery(id+"F0.wireOp",EDGE,"E12"),sQuery(id+"F0.wireOp",EDGE,"E13"),sQuery(id+"F0.wireOp",EDGE,"E14"),sQuery(id+"F0.wireOp",EDGE,"E15"),sQuery(id+"F0.wireOp",EDGE,"E17.filletArc"),sQuery(id+"F0.wireOp",EDGE,"E18.filletArc"),sQuery(id+"F0.wireOp",EDGE,"E19.filletArc"),sQuery(id+"F0.wireOp",EDGE,"E20.filletArc"),sQuery(id+"F0.wireOp",EDGE,"E25.0"),sQuery(id+"F0.wireOp",EDGE,"E25.1"),sQuery(id+"F0.wireOp",EDGE,"E25.2"),sQuery(id+"F0.wireOp",EDGE,"E25.3"),sQuery(id+"F0.wireOp",EDGE,"E25.4"),sQuery(id+"F0.wireOp",EDGE,"E25.5"),sQuery(id+"F0.wireOp",EDGE,"E25.6"),sQuery(id+"F0.wireOp",EDGE,"E25.7")])],"isStart":false});
            extrude(context, id + "F17", {"entities" : qUnion([Q0, Q1, Q2]), "endBound" : BoundingType.UP_TO_SURFACE, "endBoundEntityFace" : qUnion([Q3]), "depth" : 25 * mm});
        }
    });
